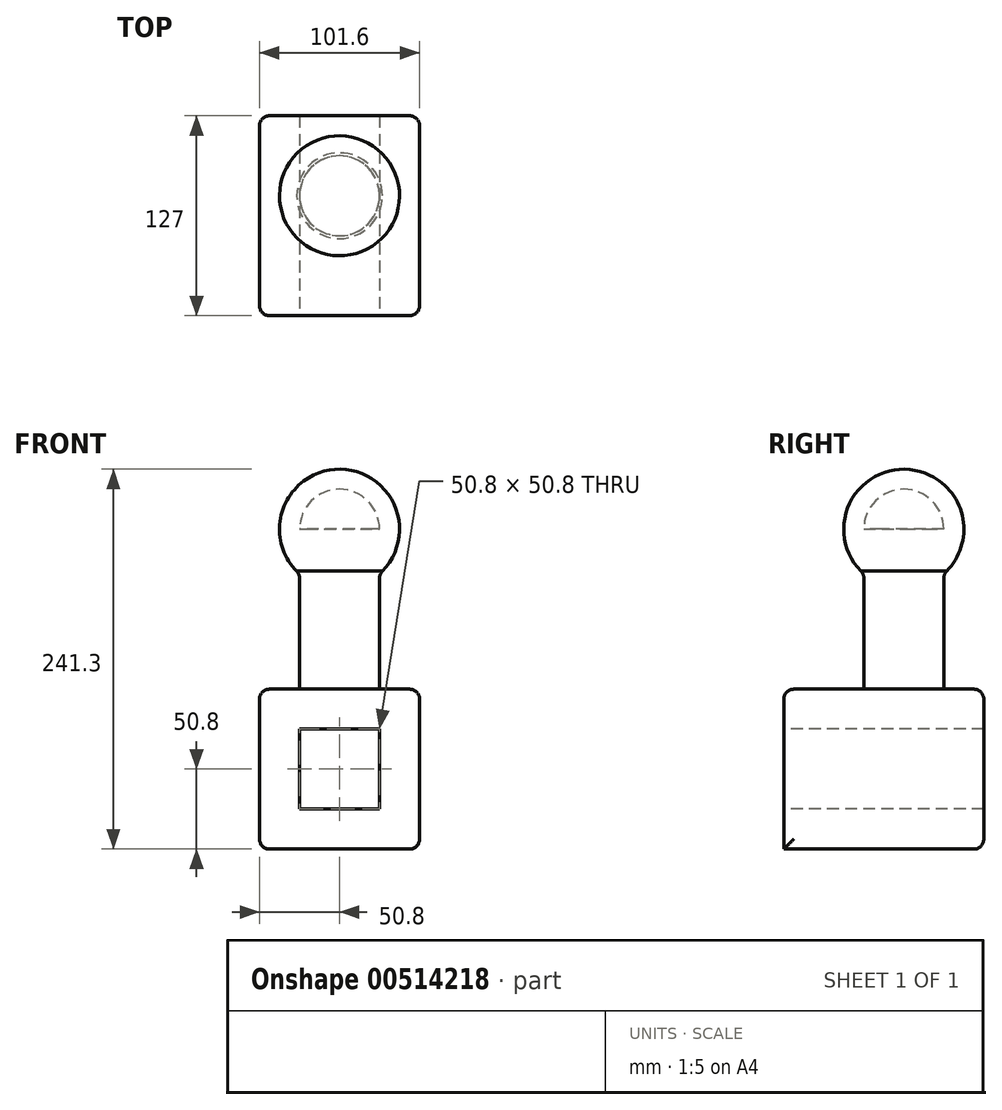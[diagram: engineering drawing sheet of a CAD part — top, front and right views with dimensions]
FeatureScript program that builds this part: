
annotation { "Feature Type Name" : "Feature", "Feature Type Description" : "" }
export const myFeature = defineFeature(function(context is Context, id is Id, definition is map)
    precondition{}
    {
        {
            var Q0;
            Q0=qCreatedBy(makeId("Top.planeOp"),FACE);
            var sketch = newSketch(context, id + "F0", { "sketchPlane" : qUnion([Q0])});
            skLineSegment(sketch, "E0.bottom", {"start": v(50.8, -50.8) * mm, "end": v(-50.8, -50.8) * mm});
            skLineSegment(sketch, "E0.top", {"start": v(50.8, 50.8) * mm, "end": v(-50.8, 50.8) * mm});
            skLineSegment(sketch, "E0.left", {"start": v(50.8, -50.8) * mm, "end": v(50.8, 50.8) * mm});
            skLineSegment(sketch, "E0.right", {"start": v(-50.8, -50.8) * mm, "end": v(-50.8, 50.8) * mm});
            skPoint(sketch, "E0.middle", {"position": v(0, 0) * mm});
            skSolve(sketch);
        }
        {
            var Q0;
            Q0 = qSketchRegion(id + "F0", true);
            extrude(context, id + "F1", {"entities" : qUnion([Q0]), "depth" : 101.6 * mm, "offsetDistance" : 25.4 * mm});
        }
        {
            var Q0;
            Q0=makeQuery(id+"F1.opExtrude","CAP_FACE",FACE,{"disambiguationData":[OSD([sQuery(id+"F0.wireOp",EDGE,"E0.bottom"),sQuery(id+"F0.wireOp",EDGE,"E0.top"),sQuery(id+"F0.wireOp",EDGE,"E0.left"),sQuery(id+"F0.wireOp",EDGE,"E0.right")])],"isStart":false});
            var sketch = newSketch(context, id + "F2", { "sketchPlane" : qUnion([Q0])});
            skCircle(sketch, "E1", {"center": v(0, 0) * mm, "radius": 25.4 * mm});
            skSolve(sketch);
        }
        {
            var Q0;
            Q0=makeQuery(id+"F2.imprint","IMPRINT",FACE,{"disambiguationData":[TD([[makeQuery(id+"F2.imprint","IMPRINT",EDGE,{"derivedFrom":sQuery(id+"F2.wireOp",EDGE,"E1")}),1.0]])]});
            extrude(context, id + "F3", {"entities" : qUnion([Q0]), "operationType" : NewBodyOperationType.ADD, "depth" : 101.6 * mm, "offsetDistance" : 25.4 * mm});
        }
        {
            var Q0;
            Q0=makeQuery(id+"F3.opExtrude","CAP_FACE",FACE,{"disambiguationData":[OSD([sQuery(id+"F2.wireOp",EDGE,"E1")])],"isStart":false});
            var sketch = newSketch(context, id + "F4", { "sketchPlane" : qUnion([Q0])});
            skArc(sketch, "E2", {"start": v(-31.83, -20.93) * mm, "mid": v(20.93, -31.83) * mm, "end": v(31.83, 20.93) * mm});
            skLineSegment(sketch, "E3", {"start": v(31.83, 20.93) * mm, "end": v(-31.83, -20.93) * mm});
            skSolve(sketch);
        }
        {
            var Q0;
            {var subQ0=sQuery(id+"F4.wireOp",EDGE,"E2");Q0=makeQuery(id+"F4.imprint","IMPRINT",FACE,{"disambiguationData":[TD([[makeQuery(id+"F4.imprint","IMPRINT",EDGE,{"derivedFrom":subQ0}),1.0]])]});}
            var Q1;
            Q1=sQuery(id+"F4.wireOp",EDGE,"E3");
            revolve(context, id + "F5", {"operationType" : NewBodyOperationType.ADD, "entities" : qUnion([Q0]), "axis" : qUnion([Q1]), "revolveType" : RevolveType.FULL});
        }
        {
            var Q0;
            Q0=makeQuery(id+"F1.opExtrude","SWEPT_FACE",FACE,{"disambiguationData":[OSD([sQuery(id+"F0.wireOp",EDGE,"E0.bottom")])]});
            var sketch = newSketch(context, id + "F6", { "sketchPlane" : qUnion([Q0])});
            skLineSegment(sketch, "E4.bottom", {"start": v(25.4, 25.4) * mm, "end": v(-25.4, 25.4) * mm});
            skLineSegment(sketch, "E4.top", {"start": v(25.4, 76.2) * mm, "end": v(-25.4, 76.2) * mm});
            skLineSegment(sketch, "E4.left", {"start": v(25.4, 25.4) * mm, "end": v(25.4, 76.2) * mm});
            skLineSegment(sketch, "E4.right", {"start": v(-25.4, 25.4) * mm, "end": v(-25.4, 76.2) * mm});
            skPoint(sketch, "E4.middle", {"position": v(0, 50.8) * mm});
            skPoint(sketch, "E4.middle.positionSnap0", {"position": v(50.8, 50.8) * mm});
            skPoint(sketch, "E4.centerSnap0", {"position": v(50.8, 50.8) * mm});
            skSolve(sketch);
        }
        {
            var Q0;
            Q0=makeQuery(id+"F6.imprint","IMPRINT",FACE,{"disambiguationData":[TD([[makeQuery(id+"F6.imprint","IMPRINT",EDGE,{"derivedFrom":sQuery(id+"F6.wireOp",EDGE,"E4.bottom")}),1.0]])]});
            var Q1;
            Q1=makeQuery(id+"F6.imprint","IMPRINT",FACE,{"disambiguationData":[TD([[makeQuery(id+"F6.imprint","IMPRINT",EDGE,{"derivedFrom":sQuery(id+"F6.wireOp",EDGE,"E4.bottom")}),-1.0]])]});
            extrude(context, id + "F7", {"entities" : qUnion([Q0, Q1]), "operationType" : NewBodyOperationType.ADD, "depth" : 25.4 * mm, "offsetDistance" : 25.4 * mm});
        }
        {
            var Q0;
            Q0=makeQuery(id+"F7.opExtrude","CAP_FACE",FACE,{"disambiguationData":[OSD([sQuery(id+"F0.wireOp",EDGE,"E0.bottom"),sQuery(id+"F0.wireOp",EDGE,"E0.left"),sQuery(id+"F0.wireOp",EDGE,"E0.right")])],"isStart":false});
            var sketch = newSketch(context, id + "F8", { "sketchPlane" : qUnion([Q0])});
            skLineSegment(sketch, "E5.bottom", {"start": v(25.4, 25.4) * mm, "end": v(-25.4, 25.4) * mm});
            skLineSegment(sketch, "E5.top", {"start": v(25.4, 76.2) * mm, "end": v(-25.4, 76.2) * mm});
            skLineSegment(sketch, "E5.left", {"start": v(25.4, 25.4) * mm, "end": v(25.4, 76.2) * mm});
            skLineSegment(sketch, "E5.right", {"start": v(-25.4, 25.4) * mm, "end": v(-25.4, 76.2) * mm});
            skPoint(sketch, "E5.middle", {"position": v(0, 50.8) * mm});
            skPoint(sketch, "E5.middle.positionSnap0", {"position": v(50.8, 50.8) * mm});
            skPoint(sketch, "E5.centerSnap0", {"position": v(50.8, 50.8) * mm});
            skSolve(sketch);
        }
        {
            var Q0;
            Q0=makeQuery(id+"F8.imprint","IMPRINT",FACE,{"disambiguationData":[TD([[makeQuery(id+"F8.imprint","IMPRINT",EDGE,{"derivedFrom":sQuery(id+"F8.wireOp",EDGE,"E5.bottom")}),-1.0]])]});
            extrude(context, id + "F9", {"entities" : qUnion([Q0]), "operationType" : NewBodyOperationType.REMOVE, "oppositeDirection" : true, "depth" : 101.6 * mm, "offsetDistance" : 25.4 * mm});
        }
        {
            var Q0;
            Q0=makeQuery(id+"F1.opExtrude","SWEPT_FACE",FACE,{"disambiguationData":[OSD([sQuery(id+"F0.wireOp",EDGE,"E0.top")])]});
            var sketch = newSketch(context, id + "F10", { "sketchPlane" : qUnion([Q0])});
            skLineSegment(sketch, "E6.bottom", {"start": v(25.4, 25.4) * mm, "end": v(-25.4, 25.4) * mm});
            skLineSegment(sketch, "E6.top", {"start": v(25.4, 76.2) * mm, "end": v(-25.4, 76.2) * mm});
            skLineSegment(sketch, "E6.left", {"start": v(25.4, 25.4) * mm, "end": v(25.4, 76.2) * mm});
            skLineSegment(sketch, "E6.right", {"start": v(-25.4, 25.4) * mm, "end": v(-25.4, 76.2) * mm});
            skPoint(sketch, "E6.middle", {"position": v(0, 50.8) * mm});
            skPoint(sketch, "E6.middle.positionSnap0", {"position": v(-50.8, 50.8) * mm});
            skPoint(sketch, "E6.centerSnap0", {"position": v(-50.8, 50.8) * mm});
            skSolve(sketch);
        }
        {
            var Q0;
            Q0 = qSketchRegion(id + "F10", true);
            extrude(context, id + "F11", {"entities" : qUnion([Q0]), "operationType" : NewBodyOperationType.REMOVE, "oppositeDirection" : true, "depth" : 101.6 * mm, "offsetDistance" : 25.4 * mm});
        }
        {
            var Q0;
            {var subQ0=sQuery(id+"F0.wireOp",EDGE,"E0.bottom");var subQ1=sQuery(id+"F0.wireOp",EDGE,"E0.right");Q0=makeQuery(id+"F7.boolean.opBoolean","MERGE",EDGE,{"derivedFrom":[makeQuery(id+"F1.opExtrude","CAP_EDGE",EDGE,{"disambiguationData":[OSD([subQ1])],"isStart":false}),makeQuery(id+"F7.opExtrude","SWEPT_EDGE",EDGE,{"disambiguationData":[OSD([subQ0,subQ1]),TDD([makeQuery(id+"F6.imprint","INTERSECT",VERTEX,{"derivedFrom":[makeQuery(id+"F1.opExtrude","SWEPT_EDGE",EDGE,{"disambiguationData":[OSD([subQ0,subQ1])]}),makeQuery(id+"F1.opExtrude","CAP_EDGE",EDGE,{"disambiguationData":[OSD([subQ0])],"isStart":false})]})])]})]});}
            var Q1;
            Q1=makeQuery(id+"F1.opExtrude","CAP_EDGE",EDGE,{"disambiguationData":[OSD([sQuery(id+"F0.wireOp",EDGE,"E0.top")])],"isStart":false});
            var Q2;
            {var subQ0=sQuery(id+"F0.wireOp",EDGE,"E0.bottom");var subQ1=sQuery(id+"F0.wireOp",EDGE,"E0.left");Q2=makeQuery(id+"F7.boolean.opBoolean","MERGE",EDGE,{"derivedFrom":[makeQuery(id+"F1.opExtrude","CAP_EDGE",EDGE,{"disambiguationData":[OSD([subQ1])],"isStart":false}),makeQuery(id+"F7.opExtrude","SWEPT_EDGE",EDGE,{"disambiguationData":[OSD([subQ0,subQ1]),TDD([makeQuery(id+"F6.imprint","INTERSECT",VERTEX,{"derivedFrom":[makeQuery(id+"F1.opExtrude","SWEPT_EDGE",EDGE,{"disambiguationData":[OSD([subQ0,subQ1])]}),makeQuery(id+"F1.opExtrude","CAP_EDGE",EDGE,{"disambiguationData":[OSD([subQ0])],"isStart":false})]})])]})]});}
            var Q3;
            {var subQ0=sQuery(id+"F0.wireOp",EDGE,"E0.bottom");Q3=makeQuery(id+"F7.opExtrude","CAP_EDGE",EDGE,{"disambiguationData":[OSD([subQ0]),TDD([makeQuery(id+"F6.imprint","IMPRINT",EDGE,{"derivedFrom":makeQuery(id+"F1.opExtrude","CAP_EDGE",EDGE,{"disambiguationData":[OSD([subQ0])],"isStart":false})})])],"isStart":false});}
            var Q4;
            Q4=makeQuery(id+"F7.opExtrude","CAP_EDGE",EDGE,{"disambiguationData":[OSD([sQuery(id+"F0.wireOp",EDGE,"E0.bottom"),sQuery(id+"F0.wireOp",EDGE,"E0.right")])],"isStart":false});
            var Q5;
            Q5=makeQuery(id+"F7.opExtrude","CAP_EDGE",EDGE,{"disambiguationData":[OSD([sQuery(id+"F0.wireOp",EDGE,"E0.bottom"),sQuery(id+"F0.wireOp",EDGE,"E0.left")])],"isStart":false});
            var Q6;
            Q6=makeQuery(id+"F1.opExtrude","SWEPT_EDGE",EDGE,{"disambiguationData":[OSD([sQuery(id+"F0.wireOp",EDGE,"E0.top"),sQuery(id+"F0.wireOp",EDGE,"E0.left")])]});
            var Q7;
            Q7=makeQuery(id+"F1.opExtrude","SWEPT_EDGE",EDGE,{"disambiguationData":[OSD([sQuery(id+"F0.wireOp",EDGE,"E0.top"),sQuery(id+"F0.wireOp",EDGE,"E0.right")])]});
            var Q8;
            {var subQ0=sQuery(id+"F0.wireOp",EDGE,"E0.left");Q8=makeQuery(id+"F7.boolean.opBoolean","MERGE",FACE,{"derivedFrom":[makeQuery(id+"F1.opExtrude","SWEPT_FACE",FACE,{"disambiguationData":[OSD([subQ0])]}),makeQuery(id+"F7.opExtrude","SWEPT_FACE",FACE,{"disambiguationData":[OSD([sQuery(id+"F0.wireOp",EDGE,"E0.bottom"),subQ0])]})]});}
            var Q9;
            {var subQ0=sQuery(id+"F0.wireOp",EDGE,"E0.right");Q9=makeQuery(id+"F7.boolean.opBoolean","MERGE",FACE,{"derivedFrom":[makeQuery(id+"F1.opExtrude","SWEPT_FACE",FACE,{"disambiguationData":[OSD([subQ0])]}),makeQuery(id+"F7.opExtrude","SWEPT_FACE",FACE,{"disambiguationData":[OSD([sQuery(id+"F0.wireOp",EDGE,"E0.bottom"),subQ0])]})]});}
            var Q10;
            Q10=makeQuery(id+"F1.opExtrude","CAP_EDGE",EDGE,{"disambiguationData":[OSD([sQuery(id+"F0.wireOp",EDGE,"E0.top")])],"isStart":true});
            var Q11;
            Q11=makeQuery(id+"F3.opExtrude","CAP_EDGE",EDGE,{"disambiguationData":[OSD([sQuery(id+"F2.wireOp",EDGE,"E1")])],"isStart":true});
            var Q12;
            Q12=makeQuery(id+"F5.boolean.opBoolean","INTERSECT",EDGE,{"derivedFrom":[makeQuery(id+"F3.opExtrude","SWEPT_FACE",FACE,{"disambiguationData":[OSD([sQuery(id+"F2.wireOp",EDGE,"E1")])]}),makeQuery(id+"F5.opRevolve","SWEPT_FACE",FACE,{"disambiguationData":[OSD([sQuery(id+"F4.wireOp",EDGE,"E2")])]})]});
            fillet(context, id + "F12", {"entities" : qUnion([Q0, Q1, Q2, Q3, Q4, Q5, Q6, Q7, Q8, Q9, Q10, Q11, Q12]), "radius" : 6.35 * mm, "tangentPropagation" : true, "allowEdgeOverflow" : false});
        }
    });
